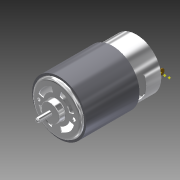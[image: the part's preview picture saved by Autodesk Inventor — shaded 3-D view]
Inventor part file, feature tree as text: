
AUTODESK INVENTOR PART (.ipt)
format: ipt  version: 2011 (Build 150239000, 239)  size: 300,032 bytes
history: native  units: mm (DEFAULTED — no unit token found)
features: sketch x17, extrude x13, other x8, plane x7, fillet x3, hole x2, mirror x2, pattern_circular x2, shell x1, chamfer x1
ambient origin geometry x8: Origin, YZ Plane, XZ Plane, XY Plane, X Axis, Y Axis, Z Axis, Center Point
bodies: Solid1 (feature_tree)
feature tree (56):
  extrude  "Extrusion1"  Depth=57.0mm TaperAngle=0.0deg
  fillet  "Fillet1"  Radius=2.0mm
  shell  "Shell1"  Thickness=0.62mm
  extrude  "Extrusion2"  Depth=4.5mm TaperAngle=0.0deg
  fillet  "Fillet2"  Radius=0.5mm
  extrude  "Extrusion3"  Depth=10.0mm TaperAngle=0.0deg
  fillet  "Fillet3"  Radius=1.6mm
  hole  "Hole1"  [1 undecoded]
  mirror  "Mirror1"
  extrude  "Extrusion4"  Depth=13.0mm
  pattern_circular  "Circular Pattern1"  Count=4 Angle=360.0deg
  plane  "Work Plane1"
  extrude  "Extrusion5"  Depth=0.62mm TaperAngle=0.0deg
  extrude  "Extrusion6"  Depth=0.62mm TaperAngle=0.0deg
  extrude  "Extrusion7"  Depth=3.0mm TaperAngle=0.0deg
  extrude  "Extrusion8"  Depth=0.8mm TaperAngle=0.0deg
  extrude  "Extrusion9"  Depth=1.0mm TaperAngle=0.0deg
  extrude  "Extrusion10"  Depth=3.15mm
  pattern_circular  "Circular Pattern2"  Count=4 Angle=360.0deg
  extrude  "Extrusion11"  Depth=0.5mm
  chamfer  "Chamfer1"  Distance=3.8mm
  hole  "Hole2"  [1 undecoded]
  mirror  "Mirror2"
  plane  "Work Plane2"
  extrude  "Extrusion12"  Depth=7.2mm TaperAngle=0.0deg
  plane  "Work Plane3"
  extrude  "Flux Ring"  Depth=1.0mm
  other  "Work Point1"
  sketch  "Sketch16"  dims[d48=6.5mm]
  sketch  "Sketch17"  dims[d49=1.0mm d50=0.0mm d51=40.0mm d53=360.0deg d54=0.5mm d55=3.8mm d56=14.0mm d57=7.2mm d58=0.0mm d59=1.0mm d60=2.0mm d61=3.0mm d62=2.0mm d63=6.0mm d64=4.0mm d65=2.0mm d66=14.3117mm d67=1.0mm d68=20.594885mm d69=18.0mm d70=10.75mm d71=5.9mm d72=9.85mm d73=7.2mm d74=0.0mm d75=45.0deg d76=1.5mm d77=38.0mm d78=0.0mm d79=3.175mm d80=6.35mm d81=3.175mm d82=6.35mm]
  other  "Work Point4"
  other  "Work Point5"
  other  "Work Point6"
  sketch  "Sketch1"  dims[d0=35.5mm d1=57.0mm d2=0.0mm d3=2.0mm d4=0.62mm]
  sketch  "Sketch2"  dims[d5=13.0mm d6=4.5mm d7=0.0mm d8=0.5mm]
  sketch  "Sketch3"  dims[d9=3.2mm d10=10.0mm d11=0.0mm d12=1.6mm]
  sketch  "Sketch4"  dims[d13=12.5mm]
  sketch  "Sketch5"  dims[d14=2.5mm d15=6.0mm d16=4.0mm d17=2.0mm d18=14.3117mm d19=8.0mm d20=20.594885mm d21=15.0deg]
  sketch  "Sketch6"  dims[d22=15.0deg d23=13.0mm]
  sketch  "Sketch7"  dims[d24=9.5mm]
  sketch  "Sketch8"  dims[d25=10.0mm d26=0.0mm d27=40.0mm d29=360.0deg]
  sketch  "Sketch9"  dims[d30=-1.75mm d31=0.62mm d32=0.0mm]
  sketch  "Sketch10"  dims[d33=24.0mm d34=0.62mm d35=0.0mm]
  sketch  "Sketch11"  dims[d36=10.75mm d37=3.0mm d38=0.0mm]
  sketch  "Sketch12"  dims[d39=6.9mm d40=0.8mm d41=0.0mm]
  sketch  "Sketch13"  dims[d42=3.2mm d43=1.0mm d44=0.0mm]
  sketch  "Sketch14"  dims[d45=3.15mm d46=3.15mm]
  sketch  "Sketch15"  dims[d47=9.875mm]
  plane  "Work Plane4"
  other  "Work Axis1"
  plane  "Work Plane5"
  other  "Work Axis2"
  plane  "Work Plane6"
  other  "Work Axis3"
  plane  "Work Plane7"
  other  "Work Axis4"
note: 2 required parameter values undecoded (feature->parameter linkage not recoverable at this tier; creation-order binding heuristic only, values carry confidence <= 0.55)
